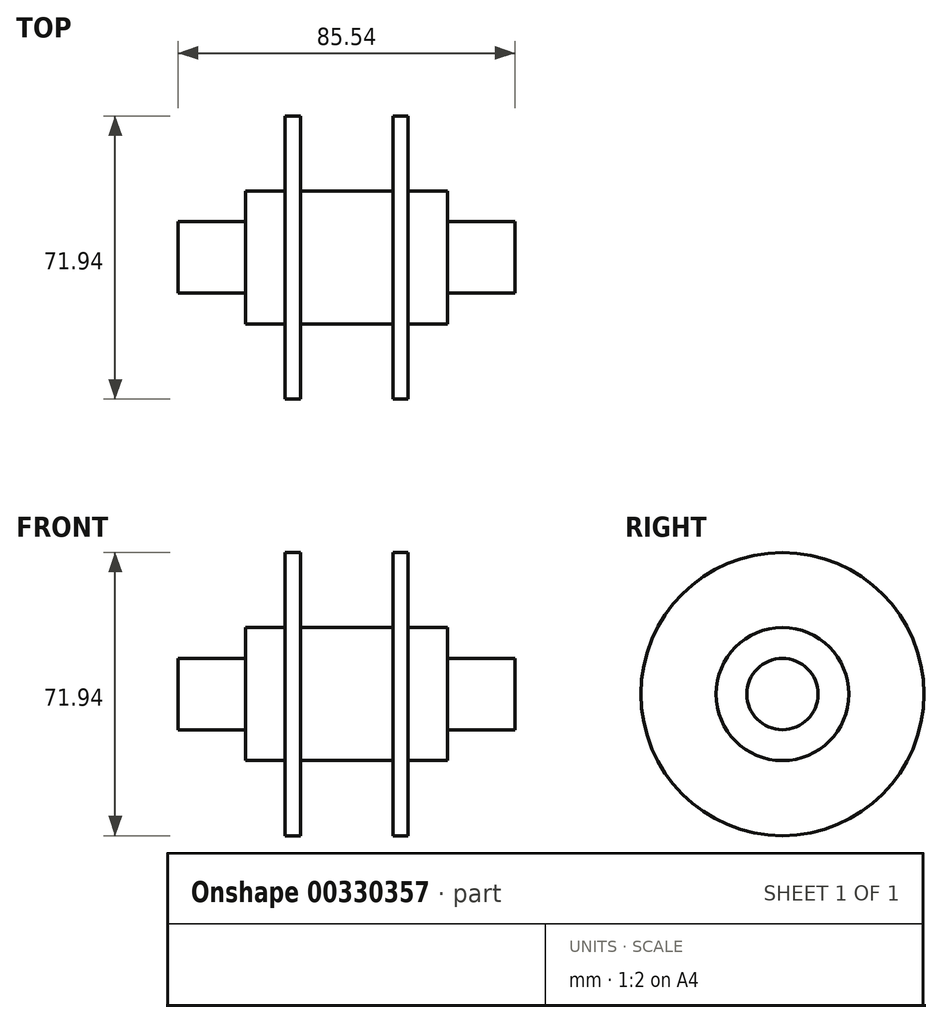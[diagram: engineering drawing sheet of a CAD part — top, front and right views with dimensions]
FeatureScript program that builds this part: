
annotation { "Feature Type Name" : "Feature", "Feature Type Description" : "" }
export const myFeature = defineFeature(function(context is Context, id is Id, definition is map)
    precondition{}
    {
        {
            var Q0;
            Q0=qCreatedBy(makeId("Front.planeOp"),FACE);
            var sketch = newSketch(context, id + "F0", { "sketchPlane" : qUnion([Q0])});
            skLineSegment(sketch, "E0", {"start": v(-42.77, 0) * mm, "end": v(-42.77, 9.05) * mm});
            skLineSegment(sketch, "E1", {"start": v(-42.77, 9.05) * mm, "end": v(-25.65, 9.05) * mm});
            skLineSegment(sketch, "E2", {"start": v(-25.65, 9.05) * mm, "end": v(-25.65, 16.88) * mm});
            skLineSegment(sketch, "E3", {"start": v(-25.65, 16.88) * mm, "end": v(-15.66, 16.88) * mm});
            skLineSegment(sketch, "E4", {"start": v(-15.66, 16.88) * mm, "end": v(-15.66, 35.97) * mm});
            skLineSegment(sketch, "E5", {"start": v(-15.66, 35.97) * mm, "end": v(-11.74, 35.97) * mm});
            skLineSegment(sketch, "E6", {"start": v(-11.74, 35.97) * mm, "end": v(-11.74, 16.88) * mm});
            skLineSegment(sketch, "E7", {"start": v(-11.74, 16.88) * mm, "end": v(0, 16.88) * mm});
            skLineSegment(sketch, "E8", {"start": v(0, 16.88) * mm, "end": v(0, 0) * mm});
            skLineSegment(sketch, "E9", {"start": v(0, 0) * mm, "end": v(-42.77, 0) * mm});
            skLineSegment(sketch, "E10.MirrorCS", {"start": v(11.74, 35.97) * mm, "end": v(11.74, 16.88) * mm});
            skLineSegment(sketch, "E11.MirrorCS", {"start": v(11.74, 16.88) * mm, "end": v(0, 16.88) * mm});
            skLineSegment(sketch, "E12.MirrorCS", {"start": v(15.66, 16.88) * mm, "end": v(15.66, 35.97) * mm});
            skLineSegment(sketch, "E13.MirrorCS", {"start": v(25.65, 16.88) * mm, "end": v(15.66, 16.88) * mm});
            skLineSegment(sketch, "E14.MirrorCS", {"start": v(25.65, 9.05) * mm, "end": v(25.65, 16.88) * mm});
            skLineSegment(sketch, "E15.MirrorCS", {"start": v(42.77, 9.05) * mm, "end": v(25.65, 9.05) * mm});
            skLineSegment(sketch, "E16.MirrorCS", {"start": v(42.77, 0) * mm, "end": v(42.77, 9.05) * mm});
            skLineSegment(sketch, "E17.MirrorCS", {"start": v(0, 0) * mm, "end": v(42.77, 0) * mm});
            skLineSegment(sketch, "E18", {"start": v(11.74, 35.97) * mm, "end": v(15.66, 35.97) * mm});
            skSolve(sketch);
        }
        {
            var Q0;
            Q0=makeQuery(id+"F0.imprint","IMPRINT",FACE,{"disambiguationData":[TD([[makeQuery(id+"F0.imprint","IMPRINT",EDGE,{"derivedFrom":sQuery(id+"F0.wireOp",EDGE,"E0")}),-1.0]])]});
            var Q1;
            Q1=makeQuery(id+"F0.imprint","IMPRINT",FACE,{"disambiguationData":[TD([[makeQuery(id+"F0.imprint","IMPRINT",EDGE,{"derivedFrom":sQuery(id+"F0.wireOp",EDGE,"E8")}),1.0]])]});
            var Q2;
            Q2=sQuery(id+"F0.wireOp",EDGE,"E9");
            revolve(context, id + "F1", {"entities" : qUnion([Q0, Q1]), "axis" : qUnion([Q2]), "revolveType" : RevolveType.FULL});
        }
    });
